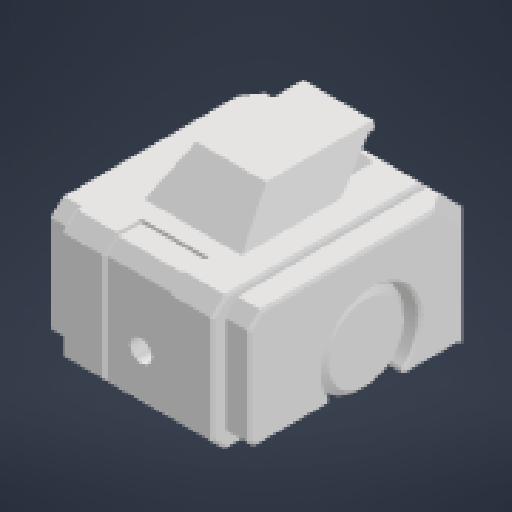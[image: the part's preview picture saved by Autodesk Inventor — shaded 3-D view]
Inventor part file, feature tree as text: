
AUTODESK INVENTOR PART (.ipt)
format: ipt  version: 2024 (Build 280153000, 153)  size: 424,960 bytes
history: native  units: in
note: dims shown in document units (in); Inventor stores cm internally (conversion verified against a paired STEP export)
features: sketch x11, extrude x10, projected_geometry x8, chamfer x7, fillet x1, mirror x1
ambient origin geometry x8: Origin, YZ Plane, XZ Plane, XY Plane, X Axis, Y Axis, Z Axis, Center Point
bodies: Solid1 (feature_tree)
feature tree (38):
  extrude  "Extrusion1"  Depth=7.2in
  chamfer  "Chamfer1"  Distance=4.3307in
  extrude  "Extrusion2"  Depth=0.1969in
  fillet  "Fillet1"  Radius=2.7402in
  chamfer  "Chamfer2"  Distance=0.7874in
  mirror  "Mirror1"
  chamfer  "Chamfer3"  Distance=0.0787in Angle=45.0deg
  extrude  "Extrusion3"  Depth=1.378in
  extrude  "Extrusion4"  Depth=4.0in TaperAngle=0.0deg
  extrude  "Extrusion5"  Depth=4.0in TaperAngle=0.0deg
  chamfer  "Chamfer4"  Angle=45.0deg  [1 undecoded]
  chamfer  "Chamfer5"  Distance=3.1496in
  extrude  "Extrusion6"  Depth=0.125in
  extrude  "Extrusion7"  Depth=0.125in
  extrude  "Extrusion8"  Depth=2.1654in TaperAngle=0.0deg
  extrude  "Extrusion9"  Depth=1.2275in
  chamfer  "Chamfer6"  Angle=45.0deg  [1 undecoded]
  sketch  "Sketch13"  dims[d28=0.1969in]
  extrude  "Extrusion10"  Depth=3.1496in TaperAngle=0.0deg
  chamfer  "Chamfer7"  Distance=3.1496in
  sketch  "Sketch1"  dims[d0=4.9213in d1=7.2in d2=4.3307in d3=0.0in]
  sketch  "Sketch4"  dims[d4=0.4375in d5=0.125in d6=45.0deg d7=0.1969in d8=2.7402in]
  projected_geometry  "Projected Loop2"
  sketch  "Sketch6"  dims[d9=0.3937in]
  sketch  "Sketch7"  dims[d10=0.1969in]
  projected_geometry  "Projected Loop5"
  sketch  "Sketch8"  dims[d11=0.5in d12=0.7874in d13=0.0in]
  sketch  "Sketch9"  dims[d14=0.125in d15=0.0787in d16=0.125in d17=45.0deg]
  projected_geometry  "Projected Loop6"
  projected_geometry  "Projected Loop7"
  sketch  "Sketch10"  dims[d18=0.0787in d19=0.125in d20=45.0deg d21=1.378in]
  projected_geometry  "Projected Loop8"
  sketch  "Sketch11"  dims[d22=1.378in d23=4.0in d24=0.0in]
  sketch  "Sketch12"  dims[d25=0.1181in d26=4.0in d27=0.0in]
  projected_geometry  "Projected Loop9"
  sketch  "Sketch14"  dims[d29=0.1969in d30=45.0deg d31=3.1496in d32=0.0in d33=0.4449in d34=0.125in d35=0.481in d36=0.4449in d37=0.125in d38=0.481in d39=2.1654in d40=0.0in d41=0.75in d42=45.0deg d43=3.1496in d44=0.0in d45=3.1496in d46=0.0in d47=0.6in d48=0.0in d49=0.2362in d50=0.125in d51=0.481in d52=0.5in d53=0.6in d54=0.0in d55=0.4449in d56=0.125in d57=0.481in d58=1.2275in d59=3.4696in]
  projected_geometry  "Projected Loop10"
  projected_geometry  "Projected Loop11"
note: 2 required parameter values undecoded (feature->parameter linkage not recoverable at this tier; creation-order binding heuristic only, values carry confidence <= 0.55)
